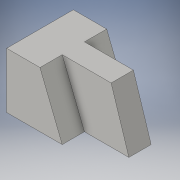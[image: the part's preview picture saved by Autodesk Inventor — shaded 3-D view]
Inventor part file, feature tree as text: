
AUTODESK INVENTOR PART (.ipt)
format: ipt  version: 2016 (Build 200138000, 138)  size: 125,952 bytes
history: native  units: in
note: dims shown in document units (in); Inventor stores cm internally (conversion verified against a paired STEP export)
features: extrude x5, sketch x5
ambient origin geometry x8: Origin, YZ Plane, XZ Plane, XY Plane, X Axis, Y Axis, Z Axis, Center Point
bodies: Solid1 (feature_tree)
feature tree (10):
  extrude  "Extrusion1"  Depth=1.25in
  sketch  "Sketch2"  dims[d2=1.5in d3=0.0in d4=0.75in]
  extrude  "Extrusion2"  Depth=1.5in
  extrude  "Extrusion3"  Depth=0.5in
  extrude  "Extrusion4"  Depth=1.0in TaperAngle=0.0deg
  extrude  "Extrusion5"  Depth=0.5in TaperAngle=0.0deg
  sketch  "Sketch1"  dims[d0=1.25in d1=1.25in]
  sketch  "Sketch3"  dims[d5=0.5in d6=0.5in]
  sketch  "Sketch4"  dims[d7=1.0in d8=0.0in d9=1.0in d10=0.0in]
  sketch  "Sketch5"  dims[d11=0.5in d12=0.0in d13=0.5in d14=0.0in]
